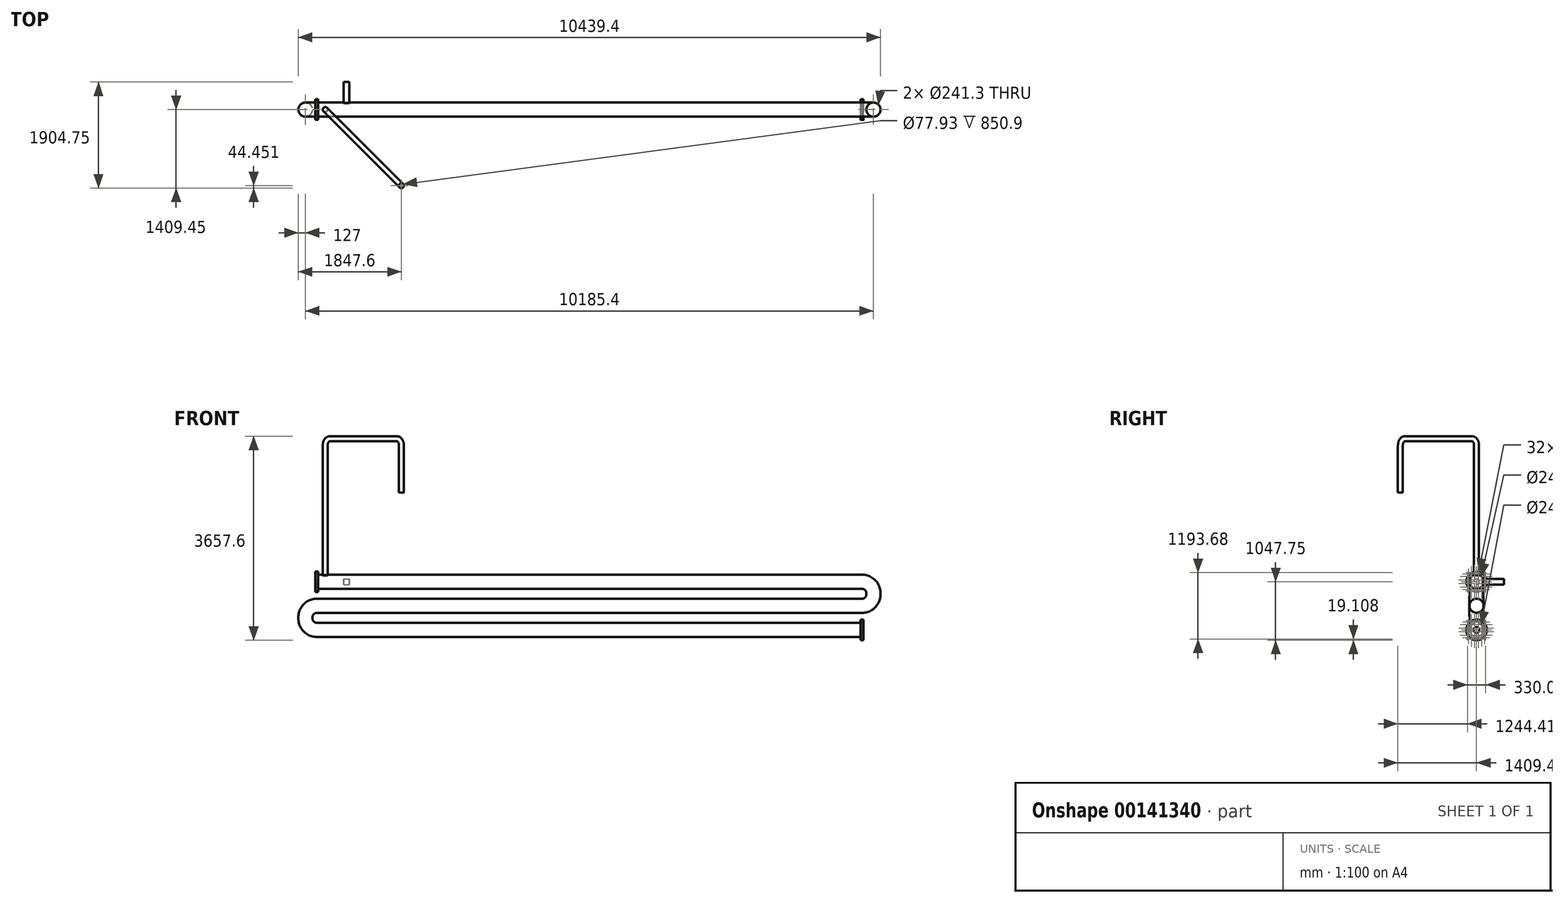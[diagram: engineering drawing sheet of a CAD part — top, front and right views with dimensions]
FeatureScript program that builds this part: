
annotation { "Feature Type Name" : "Feature", "Feature Type Description" : "" }
export const myFeature = defineFeature(function(context is Context, id is Id, definition is map)
    precondition{}
    {
        {
            var Q0;
            Q0=qCreatedBy(makeId("Front.planeOp"),FACE);
            var sketch = newSketch(context, id + "F0", { "sketchPlane" : qUnion([Q0])});
            skLineSegment(sketch, "E0", {"start": v(-4889.5, 431.8) * mm, "end": v(4889.5, 431.8) * mm});
            skLineSegment(sketch, "E1", {"start": v(5092.7, 228.6) * mm, "end": v(5092.7, 203.2) * mm});
            skLineSegment(sketch, "E2", {"start": v(4889.5, 0) * mm, "end": v(-4889.5, 0) * mm});
            skPoint(sketch, "E3.visualSharp", {"position": v(5092.7, 431.8) * mm});
            skArc(sketch, "E3.filletArc", {"start": v(5092.7, 228.6) * mm, "mid": v(5033.18, 372.28) * mm, "end": v(4889.5, 431.8) * mm});
            skPoint(sketch, "E4.visualSharp", {"position": v(5092.7, 0) * mm});
            skArc(sketch, "E4.filletArc", {"start": v(4889.5, 0) * mm, "mid": v(5033.18, 59.52) * mm, "end": v(5092.7, 203.2) * mm});
            skLineSegment(sketch, "E5", {"start": v(-4889.5, -431.8) * mm, "end": v(4890.8, -431.8) * mm});
            skLineSegment(sketch, "E6", {"start": v(-5092.7, -203.2) * mm, "end": v(-5092.7, -228.6) * mm});
            skPoint(sketch, "E7.visualSharp", {"position": v(-5092.7, 0) * mm});
            skArc(sketch, "E7.filletArc", {"start": v(-4889.5, 0) * mm, "mid": v(-5033.18, -59.52) * mm, "end": v(-5092.7, -203.2) * mm});
            skPoint(sketch, "E8.visualSharp", {"position": v(-5092.7, -431.8) * mm});
            skArc(sketch, "E8.filletArc", {"start": v(-5092.7, -228.6) * mm, "mid": v(-5033.18, -372.28) * mm, "end": v(-4889.5, -431.8) * mm});
            skSolve(sketch);
        }
        {
            var Q0;
            Q0=sQuery(id+"F0.wireOp",VERTEX,"E0.start");
            var Q1;
            Q1=sQuery(id+"F0.wireOp",EDGE,"E0");
            cPlane(context, id + "F1", {"entities" : qUnion([Q0, Q1]), "cplaneType" : CPlaneType.LINE_POINT, "offset" : 25.4 * mm, "width" : 152.4 * mm, "height" : 152.4 * mm});
        }
        {
            var Q0;
            Q0=qCreatedBy(id+"F1.planeOp",FACE);
            var sketch = newSketch(context, id + "F2", { "sketchPlane" : qUnion([Q0])});
            skPoint(sketch, "E9.0", {"position": v(0, 431.8) * mm});
            skCircle(sketch, "E10", {"center": v(0, 431.8) * mm, "radius": 127 * mm});
            skCircle(sketch, "E11", {"center": v(0, 431.8) * mm, "radius": 120.65 * mm});
            skLineSegment(sketch, "E12", {"start": v(127, 543.58) * mm, "end": v(127, 254.74) * mm, "construction": true});
            skSolve(sketch);
        }
        {
            var Q0;
            Q0=makeQuery(id+"F2.imprint","IMPRINT",FACE,{"disambiguationData":[TD([[makeQuery(id+"F2.imprint","IMPRINT",EDGE,{"derivedFrom":sQuery(id+"F2.wireOp",EDGE,"E10")}),1.0]])]});
            var Q1;
            Q1=sQuery(id+"F0.wireOp",EDGE,"E0");
            var Q2;
            Q2=sQuery(id+"F0.wireOp",EDGE,"E3.filletArc");
            var Q3;
            Q3=sQuery(id+"F0.wireOp",EDGE,"E1");
            var Q4;
            Q4=sQuery(id+"F0.wireOp",EDGE,"E4.filletArc");
            var Q5;
            Q5=sQuery(id+"F0.wireOp",EDGE,"E2");
            var Q6;
            Q6=sQuery(id+"F0.wireOp",EDGE,"E7.filletArc");
            var Q7;
            Q7=sQuery(id+"F0.wireOp",EDGE,"E6");
            var Q8;
            Q8=sQuery(id+"F0.wireOp",EDGE,"E8.filletArc");
            var Q9;
            Q9=sQuery(id+"F0.wireOp",EDGE,"E5");
            sweep(context, id + "F3", {"profiles" : qUnion([Q0]), "path" : qUnion([Q1, Q2, Q3, Q4, Q5, Q6, Q7, Q8, Q9])});
        }
        {
            var Q0;
            Q0=sQuery(id+"F2.wireOp",EDGE,"E12");
            var Q1;
            Q1=makeQuery(id+"F3.opSweep","SWEPT_FACE",FACE,{"disambiguationData":[OSD([sQuery(id+"F0.wireOp",EDGE,"E0"),sQuery(id+"F2.wireOp",EDGE,"E11")])]});
            cPlane(context, id + "F4", {"entities" : qUnion([Q0, Q1]), "cplaneType" : CPlaneType.LINE_ANGLE, "offset" : 25.4 * mm, "angle" : 0 * degree, "width" : 152.4 * mm, "height" : 152.4 * mm});
        }
        {
            var Q0;
            {var subQ0=sQuery(id+"FAvuf7nsOfoznDb_1.wireOp",EDGE,"aHmcGoK6-FMhF-DpIm-HlGy-HBCWx7sHUM18");Q0=makeQuery(id+"FAvuf7nsOfoznDb_1.imprint","IMPRINT",FACE,{"disambiguationData":[TD([[makeQuery(id+"FAvuf7nsOfoznDb_1.imprint","IMPRINT",EDGE,{"derivedFrom":subQ0}),-1.0]])]});}
            var Q1;
            Q1=makeQuery(id+"F2.imprint","IMPRINT",FACE,{"disambiguationData":[TD([[makeQuery(id+"F2.imprint","IMPRINT",EDGE,{"derivedFrom":sQuery(id+"F2.wireOp",EDGE,"E10")}),1.0]])]});
            var Q2;
            Q2=makeQuery(id+"F2.imprint","IMPRINT",FACE,{"disambiguationData":[TD([[makeQuery(id+"F2.imprint","IMPRINT",EDGE,{"derivedFrom":sQuery(id+"F2.wireOp",EDGE,"E11")}),1.0]])]});
            var Q3;
            {var subQ0=sQuery(id+"FAvuf7nsOfoznDb_1.wireOp",EDGE,"t6IFKkcG-Q1GE-Bw0w-tozD-NzRz4wOd8nfY");var subQ1=sQuery(id+"FAvuf7nsOfoznDb_1.wireOp",EDGE,"c64c8986-5413-415e-8359-5b062a1ef5a7.0");var subQ2=makeQuery(id+"FAvuf7nsOfoznDb_1.imprint","INTERSECT",VERTEX,{"derivedFrom":[subQ1,subQ0]});Q3=makeQuery(id+"FAvuf7nsOfoznDb_1.imprint","IMPRINT",FACE,{"disambiguationData":[TD([[makeQuery(id+"FAvuf7nsOfoznDb_1.imprint","IMPRINT",EDGE,{"disambiguationData":[TD([[subQ2,1.0]])],"derivedFrom":subQ1}),1.0]])]});}
            var Q4;
            Q4=makeQuery(id+"FAvuf7nsOfoznDb_1.imprint","IMPRINT",FACE,{"disambiguationData":[TD([[makeQuery(id+"FAvuf7nsOfoznDb_1.imprint","IMPRINT",EDGE,{"derivedFrom":sQuery(id+"FAvuf7nsOfoznDb_1.wireOp",EDGE,"a1aec390-3aea-4488-869f-7daf5953016e.0")}),-1.0]])]});
            var Q5;
            {var subQ0=sQuery(id+"FAvuf7nsOfoznDb_1.wireOp",EDGE,"9d6ebd95-17b0-409f-bcdd-f3717c9a91c8.0");var subQ1=makeQuery(id+"FAvuf7nsOfoznDb_1.imprint","INTERSECT",VERTEX,{"derivedFrom":[subQ0,sQuery(id+"FAvuf7nsOfoznDb_1.wireOp",EDGE,"Spnqvf19-ylGJ-kQqj-r6zM-wLSDOSpQpx5R")]});Q5=makeQuery(id+"FAvuf7nsOfoznDb_1.imprint","IMPRINT",FACE,{"disambiguationData":[TD([[makeQuery(id+"FAvuf7nsOfoznDb_1.imprint","IMPRINT",EDGE,{"disambiguationData":[TD([[subQ1,1.0]])],"derivedFrom":subQ0}),1.0]])]});}
            extrude(context, id + "F5", {"entities" : qUnion([Q0, Q1, Q2, Q3, Q4, Q5]), "operationType" : NewBodyOperationType.ADD, "depth" : 25.4 * mm});
        }
        {
            var Q0;
            Q0=sQuery(id+"F2.wireOp",VERTEX,"E9.0");
            var Q1;
            Q1=sQuery(id+"F0.wireOp",EDGE,"E0");
            cPlane(context, id + "F6", {"entities" : qUnion([Q0, Q1]), "cplaneType" : CPlaneType.LINE_POINT, "offset" : 152.4 * mm, "width" : 152.4 * mm, "height" : 152.4 * mm});
        }
        {
            var Q0;
            Q0=qCreatedBy(id+"F6.planeOp",FACE);
            cPlane(context, id + "F7", {"entities" : qUnion([Q0]), "cplaneType" : CPlaneType.OFFSET, "offset" : 152.4 * mm, "width" : 152.4 * mm, "height" : 152.4 * mm});
        }
        {
            var Q0;
            Q0=qCreatedBy(id+"F7.planeOp",FACE);
            var sketch = newSketch(context, id + "F8", { "sketchPlane" : qUnion([Q0])});
            skCircle(sketch, "E13.0", {"center": v(0, 431.8) * mm, "radius": 127 * mm});
            skLineSegment(sketch, "E14", {"start": v(-156.22, 558.8) * mm, "end": v(196.67, 558.8) * mm, "construction": true});
            skSolve(sketch);
        }
        {
            var Q0;
            Q0=sQuery(id+"F8.wireOp",EDGE,"E14");
            var Q1;
            Q1=sQuery(id+"F0.wireOp",EDGE,"E0");
            cPlane(context, id + "F9", {"entities" : qUnion([Q0, Q1]), "cplaneType" : CPlaneType.LINE_ANGLE, "offset" : 25.4 * mm, "angle" : 0 * degree, "width" : 152.4 * mm, "height" : 152.4 * mm});
        }
        {
            var Q0;
            Q0=qCreatedBy(id+"F9.planeOp",FACE);
            var sketch = newSketch(context, id + "F10", { "sketchPlane" : qUnion([Q0])});
            skPoint(sketch, "E15.0", {"position": v(-4737.1, 0) * mm});
            skCircle(sketch, "E16", {"center": v(-4737.1, 0) * mm, "radius": 44.45 * mm});
            skCircle(sketch, "E17", {"center": v(-4737.1, 0) * mm, "radius": 38.96 * mm});
            skSolve(sketch);
        }
        {
            var Q0;
            Q0=sQuery(id+"F0.wireOp",EDGE,"E0");
            var Q1;
            Q1=qCreatedBy(id+"F4.planeOp",FACE);
            cPlane(context, id + "F11", {"entities" : qUnion([Q0, Q1]), "cplaneType" : CPlaneType.LINE_ANGLE, "offset" : 25.4 * mm, "angle" : 0 * degree, "width" : 152.4 * mm, "height" : 152.4 * mm});
        }
        {
            var Q0;
            Q0=qCreatedBy(id+"F11.planeOp",FACE);
            var sketch = newSketch(context, id + "F12", { "sketchPlane" : qUnion([Q0])});
            skPoint(sketch, "E18.0", {"position": v(-4737.1, 558.8) * mm});
            skLineSegment(sketch, "E19", {"start": v(-4737.1, 558.8) * mm, "end": v(-4737.1, 2997.2) * mm, "construction": true});
            skSolve(sketch);
        }
        {
            var Q0;
            Q0=sQuery(id+"F12.wireOp",EDGE,"E19");
            var Q1;
            Q1=sQuery(id+"F0.wireOp",EDGE,"E0");
            cPlane(context, id + "F13", {"entities" : qUnion([Q0, Q1]), "cplaneType" : CPlaneType.LINE_ANGLE, "offset" : 25.4 * mm, "angle" : 135 * degree, "width" : 152.4 * mm, "height" : 152.4 * mm});
        }
        {
            var Q0;
            Q0=qCreatedBy(id+"F13.planeOp",FACE);
            var sketch = newSketch(context, id + "F14", { "sketchPlane" : qUnion([Q0])});
            skPoint(sketch, "E20.0", {"position": v(-3349.64, 558.8) * mm});
            skLineSegment(sketch, "E21", {"start": v(-3349.64, 558.8) * mm, "end": v(-3349.64, 2882.9) * mm});
            skLineSegment(sketch, "E22", {"start": v(-3235.34, 2997.2) * mm, "end": v(-1533.54, 2997.2) * mm});
            skLineSegment(sketch, "E23", {"start": v(-1419.24, 2882.9) * mm, "end": v(-1419.24, 2032) * mm});
            skPoint(sketch, "E24.visualSharp", {"position": v(-3349.64, 2997.2) * mm});
            skArc(sketch, "E24.filletArc", {"start": v(-3235.34, 2997.2) * mm, "mid": v(-3316.16, 2963.72) * mm, "end": v(-3349.64, 2882.9) * mm});
            skPoint(sketch, "E25.visualSharp", {"position": v(-1419.24, 2997.2) * mm});
            skArc(sketch, "E25.filletArc", {"start": v(-1419.24, 2882.9) * mm, "mid": v(-1452.71, 2963.72) * mm, "end": v(-1533.54, 2997.2) * mm});
            skSolve(sketch);
        }
        {
            var Q0;
            Q0=makeQuery(id+"F10.imprint","IMPRINT",FACE,{"disambiguationData":[TD([[makeQuery(id+"F10.imprint","IMPRINT",EDGE,{"derivedFrom":sQuery(id+"F10.wireOp",EDGE,"E16")}),1.0]])]});
            var Q1;
            Q1=makeQuery(id+"F3.opSweep","SWEPT_FACE",FACE,{"disambiguationData":[OSD([sQuery(id+"F0.wireOp",EDGE,"E0"),sQuery(id+"F2.wireOp",EDGE,"E10")])]});
            var Q2;
            Q2=makeQuery(id+"F3.opSweep","SWEPT_BODY",BODY,{"disambiguationData":[OSD([sQuery(id+"F0.wireOp",EDGE,"E2"),sQuery(id+"F2.wireOp",EDGE,"E11")])]});
            extrude(context, id + "F15", {"entities" : qUnion([Q0]), "operationType" : NewBodyOperationType.ADD, "endBoundEntityFace" : qUnion([Q1]), "endBoundEntityBody" : qUnion([Q2]), "depth" : 25.4 * mm});
        }
        {
            var Q0;
            Q0=makeQuery(id+"F10.imprint","IMPRINT",FACE,{"disambiguationData":[TD([[makeQuery(id+"F10.imprint","IMPRINT",EDGE,{"derivedFrom":sQuery(id+"F10.wireOp",EDGE,"E16")}),1.0]])]});
            var Q1;
            Q1=sQuery(id+"F14.wireOp",EDGE,"E21");
            var Q2;
            Q2=sQuery(id+"F14.wireOp",EDGE,"E24.filletArc");
            var Q3;
            Q3=sQuery(id+"F14.wireOp",EDGE,"E22");
            var Q4;
            Q4=sQuery(id+"F14.wireOp",EDGE,"E25.filletArc");
            var Q5;
            Q5=sQuery(id+"F14.wireOp",EDGE,"E23");
            sweep(context, id + "F16", {"operationType" : NewBodyOperationType.ADD, "profiles" : qUnion([Q0]), "path" : qUnion([Q1, Q2, Q3, Q4, Q5])});
        }
        {
            var Q0;
            Q0=makeQuery(id+"F2.imprint","IMPRINT",FACE,{"disambiguationData":[TD([[makeQuery(id+"F2.imprint","IMPRINT",EDGE,{"derivedFrom":sQuery(id+"F2.wireOp",EDGE,"E11")}),1.0]])]});
            var sketch = newSketch(context, id + "F17", { "sketchPlane" : qUnion([Q0])});
            skCircle(sketch, "E26.0.0", {"center": v(0, 431.8) * mm, "radius": 127 * mm});
            skCircle(sketch, "E27", {"center": v(0, 431.8) * mm, "radius": 184.15 * mm});
            skCircle(sketch, "E28", {"center": v(0, 431.8) * mm, "radius": 168.28 * mm, "construction": true});
            skCircle(sketch, "E29", {"center": v(32.83, 596.84) * mm, "radius": 7.94 * mm});
            skCircle(sketch, "E30.1.0", {"center": v(-32.83, 596.84) * mm, "radius": 7.94 * mm});
            skCircle(sketch, "E30.2.0", {"center": v(-93.49, 571.72) * mm, "radius": 7.94 * mm});
            skCircle(sketch, "E30.3.0", {"center": v(-139.92, 525.29) * mm, "radius": 7.94 * mm});
            skCircle(sketch, "E30.4.0", {"center": v(-165.04, 464.63) * mm, "radius": 7.94 * mm});
            skCircle(sketch, "E30.5.0", {"center": v(-165.04, 398.97) * mm, "radius": 7.94 * mm});
            skCircle(sketch, "E30.6.0", {"center": v(-139.92, 338.31) * mm, "radius": 7.94 * mm});
            skCircle(sketch, "E30.7.0", {"center": v(-93.49, 291.88) * mm, "radius": 7.94 * mm});
            skCircle(sketch, "E30.8.0", {"center": v(-32.83, 266.76) * mm, "radius": 7.94 * mm});
            skCircle(sketch, "E30.9.0", {"center": v(32.83, 266.76) * mm, "radius": 7.94 * mm});
            skCircle(sketch, "E30.10.0", {"center": v(93.49, 291.88) * mm, "radius": 7.94 * mm});
            skCircle(sketch, "E30.11.0", {"center": v(139.92, 338.31) * mm, "radius": 7.94 * mm});
            skCircle(sketch, "E30.12.0", {"center": v(165.04, 398.97) * mm, "radius": 7.94 * mm});
            skCircle(sketch, "E30.13.0", {"center": v(165.04, 464.63) * mm, "radius": 7.94 * mm});
            skCircle(sketch, "E30.14.0", {"center": v(139.92, 525.29) * mm, "radius": 7.94 * mm});
            skCircle(sketch, "E30.15.0", {"center": v(93.49, 571.72) * mm, "radius": 7.94 * mm});
            skLineSegment(sketch, "E31", {"start": v(32.83, 596.84) * mm, "end": v(-32.83, 596.84) * mm, "construction": true});
            skSolve(sketch);
        }
        {
            var Q0;
            Q0=makeQuery(id+"F17.imprint","IMPRINT",FACE,{"disambiguationData":[TD([[makeQuery(id+"F17.imprint","IMPRINT",EDGE,{"derivedFrom":sQuery(id+"F17.wireOp",EDGE,"E26.0.0")}),-1.0]])]});
            extrude(context, id + "F18", {"entities" : qUnion([Q0]), "operationType" : NewBodyOperationType.ADD, "depth" : 25.4 * mm});
        }
        {
            var Q0;
            {var subQ0=sQuery(id+"F2.wireOp",EDGE,"E10");Q0=makeQuery(id+"F18.boolean.opBoolean","MERGE",FACE,{"derivedFrom":[makeQuery(id+"F5.boolean.opBoolean","MERGE",FACE,{"derivedFrom":[makeQuery(id+"F3.opSweep","CAP_FACE",FACE,{"disambiguationData":[OSD([sQuery(id+"F0.wireOp",VERTEX,"E0.start"),subQ0,sQuery(id+"F2.wireOp",EDGE,"E11")])],"isStart":true}),makeQuery(id+"F5.opExtrude","CAP_FACE",FACE,{"disambiguationData":[OSD([subQ0])],"isStart":true})]}),makeQuery(id+"F18.opExtrude","CAP_FACE",FACE,{"disambiguationData":[OSD([sQuery(id+"F17.wireOp",EDGE,"E26.0.0"),sQuery(id+"F17.wireOp",EDGE,"E27"),sQuery(id+"F17.wireOp",EDGE,"E29"),sQuery(id+"F17.wireOp",EDGE,"E30.1.0"),sQuery(id+"F17.wireOp",EDGE,"E30.2.0"),sQuery(id+"F17.wireOp",EDGE,"E30.3.0"),sQuery(id+"F17.wireOp",EDGE,"E30.4.0"),sQuery(id+"F17.wireOp",EDGE,"E30.5.0"),sQuery(id+"F17.wireOp",EDGE,"E30.6.0"),sQuery(id+"F17.wireOp",EDGE,"E30.7.0"),sQuery(id+"F17.wireOp",EDGE,"E30.8.0"),sQuery(id+"F17.wireOp",EDGE,"E30.9.0"),sQuery(id+"F17.wireOp",EDGE,"E30.10.0"),sQuery(id+"F17.wireOp",EDGE,"E30.11.0"),sQuery(id+"F17.wireOp",EDGE,"E30.12.0"),sQuery(id+"F17.wireOp",EDGE,"E30.13.0"),sQuery(id+"F17.wireOp",EDGE,"E30.14.0"),sQuery(id+"F17.wireOp",EDGE,"E30.15.0")])],"isStart":true})]});}
            var sketch = newSketch(context, id + "F19", { "sketchPlane" : qUnion([Q0])});
            skCircle(sketch, "E32", {"center": v(0, 431.8) * mm, "radius": 50.77 * mm});
            skCircle(sketch, "E33.0", {"center": v(0, 431.8) * mm, "radius": 184.15 * mm});
            skCircle(sketch, "E34.0", {"center": v(-139.92, 525.29) * mm, "radius": 7.94 * mm});
            skCircle(sketch, "E35.0", {"center": v(-93.49, 571.72) * mm, "radius": 7.94 * mm});
            skCircle(sketch, "E36.0", {"center": v(-32.83, 596.84) * mm, "radius": 7.94 * mm});
            skCircle(sketch, "E37.0", {"center": v(32.83, 596.84) * mm, "radius": 7.94 * mm});
            skCircle(sketch, "E38.0", {"center": v(93.49, 571.72) * mm, "radius": 7.94 * mm});
            skCircle(sketch, "E39.0", {"center": v(139.92, 525.29) * mm, "radius": 7.94 * mm});
            skCircle(sketch, "E40.0", {"center": v(165.04, 464.63) * mm, "radius": 7.94 * mm});
            skCircle(sketch, "E41.0", {"center": v(165.04, 398.97) * mm, "radius": 7.94 * mm});
            skCircle(sketch, "E42.0", {"center": v(139.92, 338.31) * mm, "radius": 7.94 * mm});
            skCircle(sketch, "E43.0", {"center": v(93.49, 291.88) * mm, "radius": 7.94 * mm});
            skCircle(sketch, "E44.0", {"center": v(32.83, 266.76) * mm, "radius": 7.94 * mm});
            skCircle(sketch, "E45.0", {"center": v(-32.83, 266.76) * mm, "radius": 7.94 * mm});
            skCircle(sketch, "E46.0", {"center": v(-93.49, 291.88) * mm, "radius": 7.94 * mm});
            skCircle(sketch, "E47.0", {"center": v(-139.92, 338.31) * mm, "radius": 7.94 * mm});
            skCircle(sketch, "E48.0", {"center": v(-165.04, 398.97) * mm, "radius": 7.94 * mm});
            skCircle(sketch, "E49.0", {"center": v(-165.04, 464.63) * mm, "radius": 7.94 * mm});
            skSolve(sketch);
        }
        {
            var Q0;
            Q0 = qSketchRegion(id + "F19", true);
            extrude(context, id + "F20", {"entities" : qUnion([Q0]), "operationType" : NewBodyOperationType.ADD, "depth" : 25.4 * mm});
        }
        {
            var Q0;
            Q0=makeQuery(id+"F3.opSweep","CAP_FACE",FACE,{"disambiguationData":[OSD([sQuery(id+"F0.wireOp",VERTEX,"E5.end"),sQuery(id+"F2.wireOp",EDGE,"E10"),sQuery(id+"F2.wireOp",EDGE,"E11")])],"isStart":false});
            var sketch = newSketch(context, id + "F21", { "sketchPlane" : qUnion([Q0])});
            skCircle(sketch, "E50.0.0", {"center": v(0, -431.8) * mm, "radius": 127 * mm});
            skCircle(sketch, "E51", {"center": v(0, -431.8) * mm, "radius": 184.15 * mm});
            skCircle(sketch, "E52", {"center": v(0, -431.8) * mm, "radius": 168.28 * mm, "construction": true});
            skCircle(sketch, "E53", {"center": v(32.83, -266.76) * mm, "radius": 7.94 * mm});
            skCircle(sketch, "E54.1.0", {"center": v(-32.83, -266.76) * mm, "radius": 7.94 * mm});
            skCircle(sketch, "E54.2.0", {"center": v(-93.49, -291.88) * mm, "radius": 7.94 * mm});
            skCircle(sketch, "E54.3.0", {"center": v(-139.92, -338.31) * mm, "radius": 7.94 * mm});
            skCircle(sketch, "E54.4.0", {"center": v(-165.04, -398.97) * mm, "radius": 7.94 * mm});
            skCircle(sketch, "E54.5.0", {"center": v(-165.04, -464.63) * mm, "radius": 7.94 * mm});
            skCircle(sketch, "E54.6.0", {"center": v(-139.92, -525.29) * mm, "radius": 7.94 * mm});
            skCircle(sketch, "E54.7.0", {"center": v(-93.49, -571.72) * mm, "radius": 7.94 * mm});
            skCircle(sketch, "E54.8.0", {"center": v(-32.83, -596.84) * mm, "radius": 7.94 * mm});
            skCircle(sketch, "E54.9.0", {"center": v(32.83, -596.84) * mm, "radius": 7.94 * mm});
            skCircle(sketch, "E54.10.0", {"center": v(93.49, -571.72) * mm, "radius": 7.94 * mm});
            skCircle(sketch, "E54.11.0", {"center": v(139.92, -525.29) * mm, "radius": 7.94 * mm});
            skCircle(sketch, "E54.12.0", {"center": v(165.04, -464.63) * mm, "radius": 7.94 * mm});
            skCircle(sketch, "E54.13.0", {"center": v(165.04, -398.97) * mm, "radius": 7.94 * mm});
            skCircle(sketch, "E54.14.0", {"center": v(139.92, -338.31) * mm, "radius": 7.94 * mm});
            skCircle(sketch, "E54.15.0", {"center": v(93.49, -291.88) * mm, "radius": 7.94 * mm});
            skLineSegment(sketch, "E55", {"start": v(32.83, -266.76) * mm, "end": v(-32.83, -266.76) * mm, "construction": true});
            skSolve(sketch);
        }
        {
            var Q0;
            Q0=makeQuery(id+"F21.imprint","IMPRINT",FACE,{"disambiguationData":[TD([[makeQuery(id+"F21.imprint","IMPRINT",EDGE,{"derivedFrom":sQuery(id+"F21.wireOp",EDGE,"E50.0.0")}),-1.0]])]});
            extrude(context, id + "F22", {"entities" : qUnion([Q0]), "operationType" : NewBodyOperationType.ADD, "oppositeDirection" : true, "depth" : 25.4 * mm});
        }
        {
            var Q0;
            Q0=makeQuery(id+"F22.boolean.opBoolean","MERGE",FACE,{"derivedFrom":[makeQuery(id+"F3.opSweep","CAP_FACE",FACE,{"disambiguationData":[OSD([sQuery(id+"F0.wireOp",VERTEX,"E5.end"),sQuery(id+"F2.wireOp",EDGE,"E10"),sQuery(id+"F2.wireOp",EDGE,"E11")])],"isStart":false}),makeQuery(id+"F22.opExtrude","CAP_FACE",FACE,{"disambiguationData":[OSD([sQuery(id+"F21.wireOp",EDGE,"E50.0.0"),sQuery(id+"F21.wireOp",EDGE,"E51"),sQuery(id+"F21.wireOp",EDGE,"E53"),sQuery(id+"F21.wireOp",EDGE,"E54.1.0"),sQuery(id+"F21.wireOp",EDGE,"E54.2.0"),sQuery(id+"F21.wireOp",EDGE,"E54.3.0"),sQuery(id+"F21.wireOp",EDGE,"E54.4.0"),sQuery(id+"F21.wireOp",EDGE,"E54.5.0"),sQuery(id+"F21.wireOp",EDGE,"E54.6.0"),sQuery(id+"F21.wireOp",EDGE,"E54.7.0"),sQuery(id+"F21.wireOp",EDGE,"E54.8.0"),sQuery(id+"F21.wireOp",EDGE,"E54.9.0"),sQuery(id+"F21.wireOp",EDGE,"E54.10.0"),sQuery(id+"F21.wireOp",EDGE,"E54.11.0"),sQuery(id+"F21.wireOp",EDGE,"E54.12.0"),sQuery(id+"F21.wireOp",EDGE,"E54.13.0"),sQuery(id+"F21.wireOp",EDGE,"E54.14.0"),sQuery(id+"F21.wireOp",EDGE,"E54.15.0")])],"isStart":true})]});
            var sketch = newSketch(context, id + "F23", { "sketchPlane" : qUnion([Q0])});
            skCircle(sketch, "E56", {"center": v(0, -431.8) * mm, "radius": 50.77 * mm});
            skCircle(sketch, "E57.0", {"center": v(0, -431.8) * mm, "radius": 184.15 * mm});
            skCircle(sketch, "E58.0", {"center": v(-93.49, -291.88) * mm, "radius": 7.94 * mm});
            skCircle(sketch, "E59.0", {"center": v(-32.83, -266.76) * mm, "radius": 7.94 * mm});
            skCircle(sketch, "E60.0", {"center": v(32.83, -266.76) * mm, "radius": 7.94 * mm});
            skCircle(sketch, "E61.0", {"center": v(93.49, -291.88) * mm, "radius": 7.94 * mm});
            skCircle(sketch, "E62.0", {"center": v(139.92, -338.31) * mm, "radius": 7.94 * mm});
            skCircle(sketch, "E63.0", {"center": v(165.04, -398.97) * mm, "radius": 7.94 * mm});
            skCircle(sketch, "E64.0", {"center": v(165.04, -464.63) * mm, "radius": 7.94 * mm});
            skCircle(sketch, "E65.0", {"center": v(139.92, -525.29) * mm, "radius": 7.94 * mm});
            skCircle(sketch, "E66.0", {"center": v(93.49, -571.72) * mm, "radius": 7.94 * mm});
            skCircle(sketch, "E67.0", {"center": v(32.83, -596.84) * mm, "radius": 7.94 * mm});
            skCircle(sketch, "E68.0", {"center": v(-32.83, -596.84) * mm, "radius": 7.94 * mm});
            skCircle(sketch, "E69.0", {"center": v(-93.49, -571.72) * mm, "radius": 7.94 * mm});
            skCircle(sketch, "E70.0", {"center": v(-139.92, -525.29) * mm, "radius": 7.94 * mm});
            skCircle(sketch, "E71.0", {"center": v(-165.04, -464.63) * mm, "radius": 7.94 * mm});
            skCircle(sketch, "E72.0", {"center": v(-165.04, -398.97) * mm, "radius": 7.94 * mm});
            skCircle(sketch, "E73.0", {"center": v(-139.92, -338.31) * mm, "radius": 7.94 * mm});
            skSolve(sketch);
        }
        {
            var Q0;
            Q0 = qSketchRegion(id + "F23", true);
            extrude(context, id + "F24", {"entities" : qUnion([Q0]), "operationType" : NewBodyOperationType.ADD, "depth" : 25.4 * mm});
        }
        {
            var Q0;
            Q0=qCreatedBy(id+"F11.planeOp",FACE);
            cPlane(context, id + "F25", {"entities" : qUnion([Q0]), "cplaneType" : CPlaneType.OFFSET, "offset" : 495.3 * mm, "oppositeDirection" : true, "width" : 152.4 * mm, "height" : 152.4 * mm});
        }
        {
            var Q0;
            Q0=qCreatedBy(id+"F4.planeOp",FACE);
            var sketch = newSketch(context, id + "F26", { "sketchPlane" : qUnion([Q0])});
            skLineSegment(sketch, "E74.0", {"start": v(4864.1, 247.65) * mm, "end": v(4864.1, 615.95) * mm});
            skLineSegment(sketch, "E75.0", {"start": v(4889.5, 431.8) * mm, "end": v(-4889.5, 431.8) * mm, "construction": true});
            skLineSegment(sketch, "E76.bottom", {"start": v(4305.3, 482.6) * mm, "end": v(4406.9, 482.6) * mm});
            skLineSegment(sketch, "E76.top", {"start": v(4305.3, 381) * mm, "end": v(4406.9, 381) * mm});
            skLineSegment(sketch, "E76.left", {"start": v(4305.3, 482.6) * mm, "end": v(4305.3, 381) * mm});
            skLineSegment(sketch, "E76.right", {"start": v(4406.9, 482.6) * mm, "end": v(4406.9, 381) * mm});
            skPoint(sketch, "E77", {"position": v(4305.3, 431.8) * mm});
            skPoint(sketch, "E78", {"position": v(4406.9, 431.8) * mm});
            skLineSegment(sketch, "E79", {"start": v(4406.9, 482.6) * mm, "end": v(4305.3, 381) * mm, "construction": true});
            skPoint(sketch, "E80", {"position": v(4356.1, 431.8) * mm});
            skSolve(sketch);
        }
        {
            var Q0;
            Q0 = qSketchRegion(id + "F26", true);
            extrude(context, id + "F27", {"entities" : qUnion([Q0]), "operationType" : NewBodyOperationType.ADD, "oppositeDirection" : true, "depth" : 25.4 * mm});
        }
        {
            var Q0;
            Q0=qCreatedBy(id+"F25.planeOp",FACE);
            var sketch = newSketch(context, id + "F28", { "sketchPlane" : qUnion([Q0])});
            skLineSegment(sketch, "E81.0.0", {"start": v(-4406.9, 381) * mm, "end": v(-4406.9, 431.8) * mm});
            skLineSegment(sketch, "E81.0.1", {"start": v(-4406.9, 431.8) * mm, "end": v(-4406.9, 482.6) * mm});
            skLineSegment(sketch, "E81.0.2", {"start": v(-4406.9, 482.6) * mm, "end": v(-4305.3, 482.6) * mm});
            skLineSegment(sketch, "E81.0.3", {"start": v(-4305.3, 482.6) * mm, "end": v(-4305.3, 431.8) * mm});
            skLineSegment(sketch, "E81.0.4", {"start": v(-4305.3, 431.8) * mm, "end": v(-4305.3, 381) * mm});
            skLineSegment(sketch, "E81.0.5", {"start": v(-4305.3, 381) * mm, "end": v(-4406.9, 381) * mm});
            skLineSegment(sketch, "E82", {"start": v(-4305.3, 482.6) * mm, "end": v(-4406.9, 381) * mm, "construction": true});
            skLineSegment(sketch, "E83", {"start": v(-4406.9, 482.6) * mm, "end": v(-4305.3, 381) * mm, "construction": true});
            skPoint(sketch, "E84", {"position": v(-4356.1, 431.8) * mm});
            skSolve(sketch);
        }
        {
            var Q0;
            Q0=makeQuery(id+"F28.imprint","IMPRINT",FACE,{"disambiguationData":[TD([[makeQuery(id+"F28.imprint","IMPRINT",EDGE,{"derivedFrom":sQuery(id+"F28.wireOp",EDGE,"E81.0.0")}),-1.0]])]});
            var Q1;
            Q1=makeQuery(id+"F3.opSweep","SWEPT_BODY",BODY,{"disambiguationData":[OSD([sQuery(id+"F0.wireOp",EDGE,"E5"),sQuery(id+"F2.wireOp",EDGE,"E10"),sQuery(id+"F2.wireOp",EDGE,"E11")])]});
            extrude(context, id + "F29", {"entities" : qUnion([Q0]), "operationType" : NewBodyOperationType.ADD, "endBound" : BoundingType.UP_TO_BODY, "endBoundEntityBody" : qUnion([Q1]), "depth" : 25.4 * mm});
        }
    });
